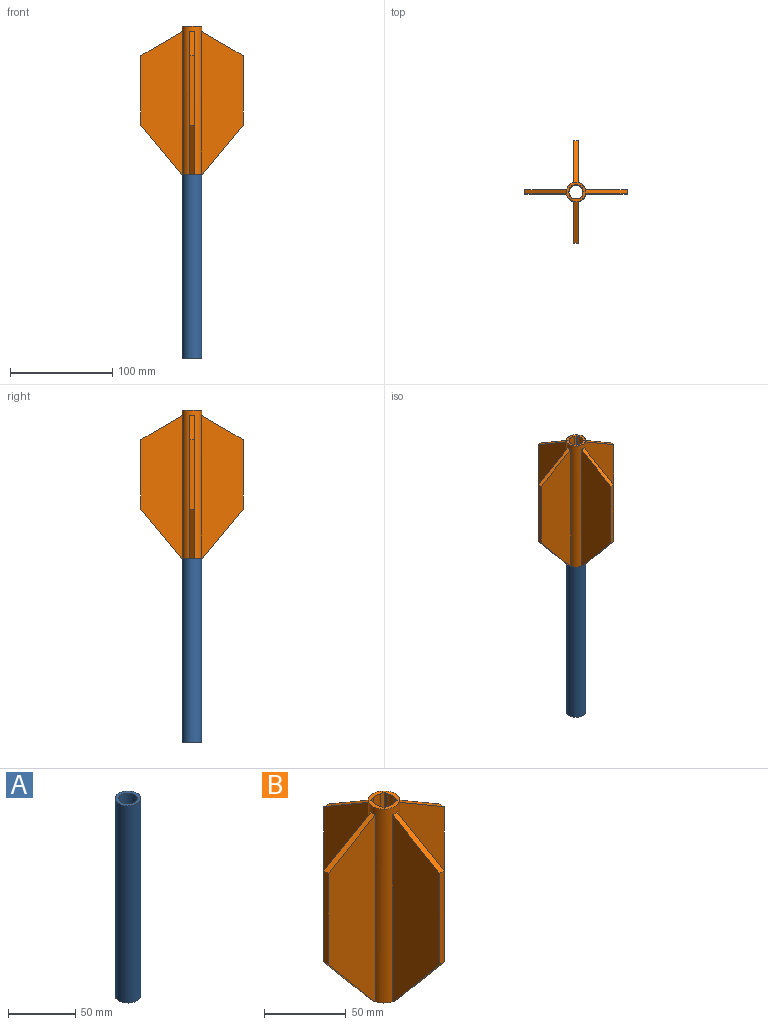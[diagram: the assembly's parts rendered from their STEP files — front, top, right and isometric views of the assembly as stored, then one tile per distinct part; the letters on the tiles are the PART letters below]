
ASSEMBLY  parts=2 mates=1
PART A: 4 faces, bbox 19.2x19.2x180 mm
  f0: cylinder r=9.6mm len=180mm, axis (0,0,-1), area 10857.3mm2, adj f1,f2
  f1: plane 19.2x19.2mm, normal (0,0,1), area 141mm2, adj f0,f3
  f2: plane 19.2x19.2mm, normal (0,0,-1), area 141mm2, adj f0,f3
  f3: cylinder r=6.88mm len=180mm, axis (0,0,1), area 7775.4mm2, adj f1,f2
PART B: 36 faces, bbox 100x100x145 mm
  f0: plane 19.2x19.2mm, normal (0,0,1), area 129.7mm2, adj f1,f23,f24,f25,f27,f28,f30,f31
  f1: cylinder r=9.6mm len=145mm, axis (0,0,-1), area 6494.7mm2, adj f0,f2,f3,f4,f6,f8,f9,f11
  f2: plane 20x20mm, normal (0,0,-1), area 148.6mm2, adj f1,f3,f4,f7,f8,f9,f12,f13
  f3: plane 139.77x40.61mm, normal (1,0,0), area 4233.5mm2, adj f1,f2,f5,f6,f7
  f4: plane 139.77x40.61mm, normal (-1,0,0), area 4233.5mm2, adj f1,f2,f5,f6,f7
  f5: plane 68x4mm, normal (0,1,0), area 272mm2, adj f3,f4,f6,f7
  f6: plane 40.61x23.77mm, normal (0,0.51,0.86), area 187.6mm2, adj f1,f3,f4,f5
  f7: plane 48x40mm, normal (0,0.77,-0.64), area 249.9mm2, adj f2,f3,f4,f5
  f8: plane 139.77x40.61mm, normal (0,1,0), area 4233.5mm2, adj f1,f2,f10,f11,f12
  f9: plane 139.77x40.61mm, normal (0,-1,0), area 4233.5mm2, adj f1,f2,f10,f11,f12
  f10: plane 68x4mm, normal (-1,0,0), area 272mm2, adj f8,f9,f11,f12
  f11: plane 40.61x23.77mm, normal (-0.51,0,0.86), area 187.6mm2, adj f1,f8,f9,f10
  f12: plane 48x40mm, normal (-0.77,0,-0.64), area 249.9mm2, adj f2,f8,f9,f10
  f13: plane 139.77x40.61mm, normal (-1,0,0), area 4233.5mm2, adj f1,f2,f15,f16,f17
  f14: plane 139.77x40.61mm, normal (1,0,0), area 4233.5mm2, adj f1,f2,f15,f16,f17
  f15: plane 68x4mm, normal (0,-1,0), area 272mm2, adj f13,f14,f16,f17
  f16: plane 40.61x23.77mm, normal (0,-0.51,0.86), area 187.6mm2, adj f1,f13,f14,f15
  f17: plane 48x40mm, normal (0,-0.77,-0.64), area 249.9mm2, adj f2,f13,f14,f15
  f18: plane 139.77x40.61mm, normal (0,-1,0), area 4233.5mm2, adj f1,f2,f20,f21,f22
  f19: plane 139.77x40.61mm, normal (0,1,0), area 4233.5mm2, adj f1,f2,f20,f21,f22
  f20: plane 68x4mm, normal (1,0,0), area 272mm2, adj f18,f19,f21,f22
  f21: plane 40.61x23.77mm, normal (0.51,0,0.86), area 187.6mm2, adj f1,f18,f19,f20
  f22: plane 48x40mm, normal (0.77,0,-0.64), area 249.9mm2, adj f2,f18,f19,f20
  f23: cylinder r=6.88mm len=145mm, axis (0,0,1), area 5733.5mm2, adj f0,f2,f24,f25,f26,f27,f28,f29
  f24: plane 35x2.64mm, normal (0,-1,0), area 92.5mm2, adj f0,f23,f25,f26
  f25: plane 35x2.64mm, normal (1,0,0), area 92.5mm2, adj f0,f23,f24,f26
  f26: plane 2.64x2.64mm, normal (0,0,1), area 2.8mm2, adj f23,f24,f25
  f27: plane 35x2.64mm, normal (0,1,0), area 92.5mm2, adj f0,f23,f28,f29
  f28: plane 35x2.64mm, normal (-1,0,0), area 92.5mm2, adj f0,f23,f27,f29
  f29: plane 2.64x2.64mm, normal (0,0,1), area 2.8mm2, adj f23,f27,f28
  f30: plane 35x2.64mm, normal (1,0,0), area 92.5mm2, adj f0,f23,f31,f32
  f31: plane 35x2.64mm, normal (0,1,0), area 92.5mm2, adj f0,f23,f30,f32
  f32: plane 2.64x2.64mm, normal (0,0,1), area 2.8mm2, adj f23,f30,f31
  f33: plane 35x2.64mm, normal (0,-1,0), area 92.5mm2, adj f0,f23,f34,f35
  f34: plane 35x2.64mm, normal (-1,0,0), area 92.5mm2, adj f0,f23,f33,f35
  f35: plane 2.64x2.64mm, normal (0,0,1), area 2.8mm2, adj f23,f33,f34
PLACE A t=(-68.96,-0.96,-219.22)mm
PLACE B t=(-68.96,-0.96,-39.22)mm
MATE fastened A.f0 <-> B.f1  axis (0,0,1) through (-68.96,-0.96,-39.22)mm
